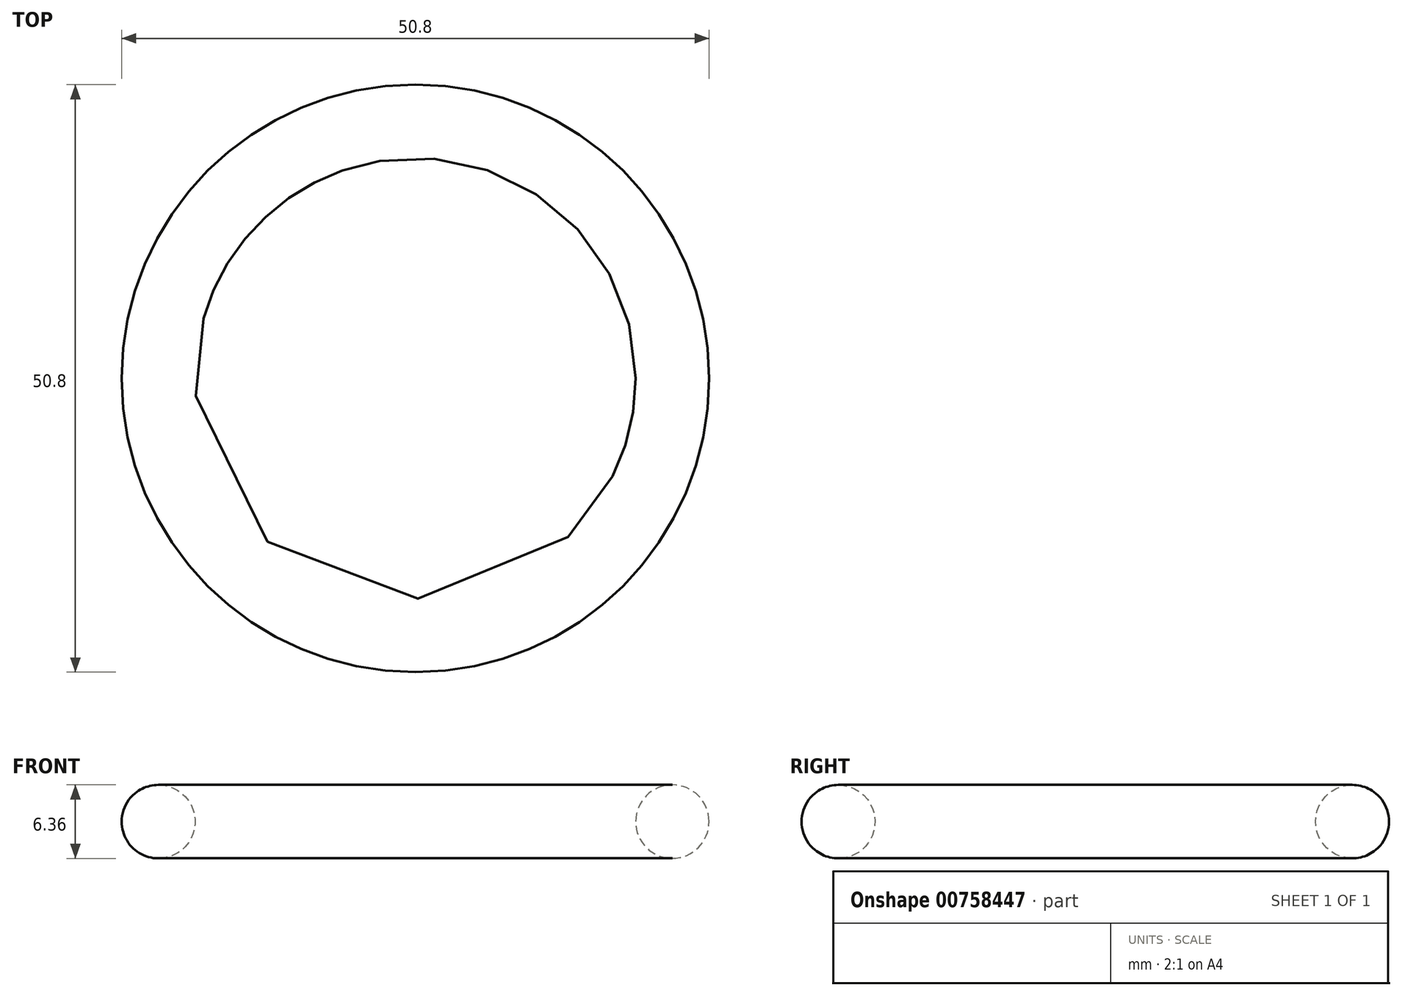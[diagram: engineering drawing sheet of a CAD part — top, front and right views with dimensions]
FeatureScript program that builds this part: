
annotation { "Feature Type Name" : "Feature", "Feature Type Description" : "" }
export const myFeature = defineFeature(function(context is Context, id is Id, definition is map)
    precondition{}
    {
        {
            var Q0;
            Q0=qCreatedBy(makeId("Front.planeOp"),FACE);
            var sketch = newSketch(context, id + "F0", { "sketchPlane" : qUnion([Q0])});
            skCircle(sketch, "E0", {"center": v(-22.22, 0) * mm, "radius": 3.18 * mm});
            skLineSegment(sketch, "E1", {"start": v(0, 29.76) * mm, "end": v(0, -43.61) * mm, "construction": true});
            skSolve(sketch);
        }
        {
            var Q0;
            Q0 = qSketchRegion(id + "F0", true);
            var Q1;
            Q1=sQuery(id+"F0.wireOp",EDGE,"E1");
            revolve(context, id + "F1", {"surfaceOperationType" : NewSurfaceOperationType.NEW, "entities" : qUnion([Q0]), "axis" : qUnion([Q1]), "revolveType" : RevolveType.FULL});
        }
    });
